# Revit family: Faucet-Bath-Handshower_Kit-KOHLER-PURIST-K-72632T_1
name_source: partatom
category: Plumbing Fixtures
revit_build: Autodesk Revit 2017 (Build: 20160225_1515(x64)
units: mm (PartAtom-declared; Revit-internal decimal feet)

## family parameters
Cut with Voids When Loaded = No
Host = Face
OmniClass Number = 23.31.11.00
Part Type = Normal
Room Calculation Point = No
Round Connector Dimension = Use Diameter
Shared = No

## types (4) — shared parameters
ADA Compliant = No
Assembly Code = D2010
CW Connection = Yes
Cold Water Inlet = Cold Water Inlet
Date Modified = 08/31/2020
Default Elevation = 36"
Description = Exposed Bath Shower Faucet
Drain Included = No
Flow Rate = 0 GPM
HW Connection = Yes
Height = 21 11/16"
Hot Water Inlet = Hot Water Inlet
Length = 8 3/16"
Manufacturer = KOHLER Co.
Master Format 2014 = 22 41 39
Master Format 2014 Name = Residential Faucets, Supplies, and Trim
Material = Premium Metal Construction
Pressure = 0.00 psi
Product Documentation Link = https://files.kohler.com.cn
Product Name = PURIST
Product Page URL = https://www.kohler.com.cn
Spout Reach = 8 3/16"
URL = http://www.kohler.com.cn
Vent Connection = No
Waste Connection = No
Waste Water Outlet = Waste Water Outlet
WaterSense Certified = No
Width = 14 3/16"

## per-type parameters (varying)
| type | Finish | Handle Clearance | Model | Sculpted Lever Handle | Straight Lever Handle | Type |
| Sculpted Lever Handle, CP-Polished Chrome | Kohler-Metal-CP-Polished_Chrome | 3" | K-72632T-4-CP | Yes | No | 1 |
| Sculpted Lever Handle, RGD-Rose Gold | Kohler-Metal-RGD-Rose_Gold | 3" | K-72632T-4-RGD | Yes | No | 2 |
| Straight Lever Handle, CP-Polished Chrome | Kohler-Metal-CP-Polished_Chrome | 3 1/4" | K-72632T-4A-CP | No | Yes | 3 |
| Straight Lever Handle, RGD-Rose Gold | Kohler-Metal-RGD-Rose_Gold | 3 1/4" | K-72632T-4A-RGD | No | Yes | 4 |

## geometry (parser evidence)
native form markers: Sweep x5
no freeform markers — native parametric forms only
